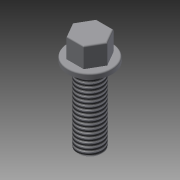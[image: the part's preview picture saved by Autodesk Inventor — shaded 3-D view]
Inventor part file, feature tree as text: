
AUTODESK INVENTOR PART (.ipt)
format: ipt  version: 2015 (Build 190159000, 159)  size: 120,320 bytes
history: native  units: mm
features: extrude x3, sketch x3, fillet x2, thread x1, chamfer x1
ambient origin geometry x8: Origin, YZ Plane, XZ Plane, XY Plane, X Axis, Y Axis, Z Axis, Center Point
bodies: 实体1 (feature_tree)
feature tree (10):
  extrude  "拉伸1"  Depth=1.0mm TaperAngle=0.0deg
  extrude  "拉伸2"  Depth=6.0mm
  extrude  "拉伸3"  Depth=5.0mm
  thread  "螺纹1"  [1 undecoded]
  chamfer  "倒角1"  Distance=10.0mm
  fillet  "圆角1"  Radius=0.25mm
  fillet  "圆角2"  Radius=0.25mm
  sketch  "草图1"  dims[d0=9.0mm d1=1.0mm d2=0.0mm]
  sketch  "草图2"  dims[d3=0.728222mm d4=6.0mm]
  sketch  "草图3"  dims[d5=4.0mm d6=0.0mm d7=5.0mm d8=15.0mm d9=0.0mm d10=10.0mm d11=0.0mm d12=0.25mm d13=2.0mm d14=45.0deg d15=0.25mm d16=0.25mm]
note: 1 required parameter value undecoded (feature->parameter linkage not recoverable at this tier; creation-order binding heuristic only, values carry confidence <= 0.55)
